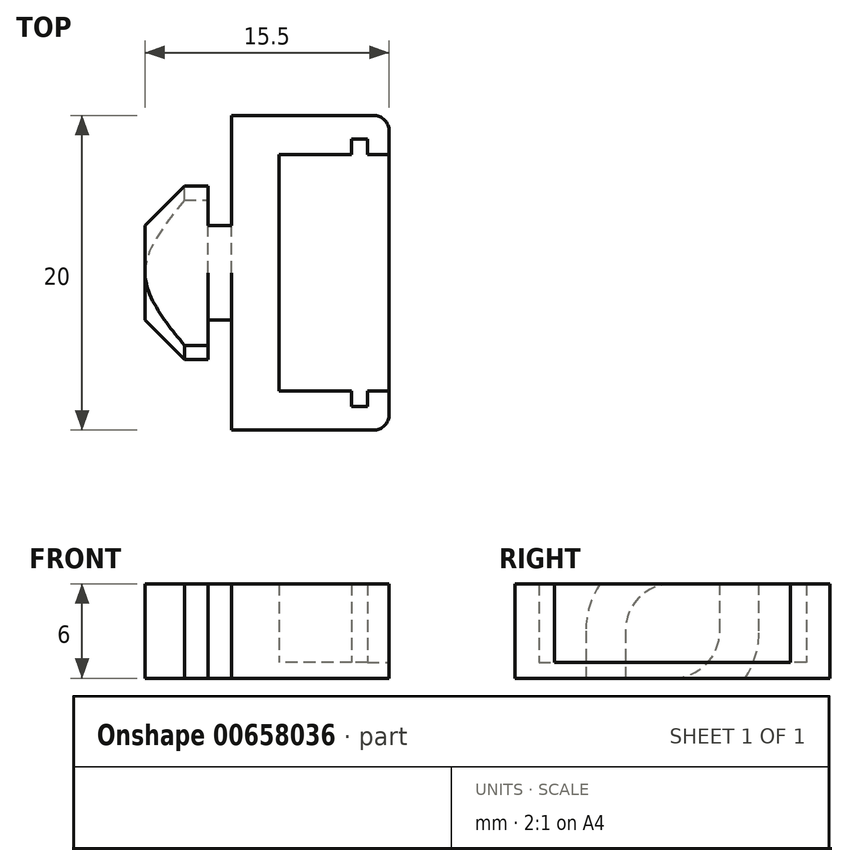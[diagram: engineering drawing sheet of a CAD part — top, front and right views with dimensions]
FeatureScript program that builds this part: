
annotation { "Feature Type Name" : "Feature", "Feature Type Description" : "" }
export const myFeature = defineFeature(function(context is Context, id is Id, definition is map)
    precondition{}
    {
        {
            var Q0;
            Q0=qCreatedBy(makeId("Top.planeOp"),FACE);
            var sketch = newSketch(context, id + "F0", { "sketchPlane" : qUnion([Q0])});
            skLineSegment(sketch, "E0.bottom", {"start": v(0, 0) * mm, "end": v(9, 0) * mm});
            skLineSegment(sketch, "E0.top", {"start": v(0, 20) * mm, "end": v(9, 20) * mm});
            skLineSegment(sketch, "E0.left", {"start": v(0, 0) * mm, "end": v(0, 7) * mm});
            skLineSegment(sketch, "E0.right", {"start": v(10, 1) * mm, "end": v(10, 2.5) * mm});
            skLineSegment(sketch, "E1", {"start": v(10, 17.5) * mm, "end": v(8.62, 17.5) * mm});
            skLineSegment(sketch, "E2", {"start": v(3, 17.5) * mm, "end": v(3, 2.5) * mm});
            skLineSegment(sketch, "E3", {"start": v(3, 2.5) * mm, "end": v(7.62, 2.5) * mm});
            skLineSegment(sketch, "E4.trimOffspring", {"start": v(10, 17.5) * mm, "end": v(10, 19) * mm});
            skLineSegment(sketch, "E5", {"start": v(7.62, 17.5) * mm, "end": v(7.62, 18.5) * mm});
            skLineSegment(sketch, "E6", {"start": v(7.62, 18.5) * mm, "end": v(8.62, 18.5) * mm});
            skLineSegment(sketch, "E7", {"start": v(8.62, 18.5) * mm, "end": v(8.62, 17.5) * mm});
            skLineSegment(sketch, "E8", {"start": v(8.62, 2.5) * mm, "end": v(8.62, 1.5) * mm});
            skLineSegment(sketch, "E9", {"start": v(8.62, 1.5) * mm, "end": v(7.62, 1.5) * mm});
            skLineSegment(sketch, "E10", {"start": v(7.62, 1.5) * mm, "end": v(7.62, 2.5) * mm});
            skLineSegment(sketch, "E11.trimOffspring", {"start": v(7.62, 17.5) * mm, "end": v(3, 17.5) * mm});
            skLineSegment(sketch, "E12.trimOffspring", {"start": v(8.62, 2.5) * mm, "end": v(10, 2.5) * mm});
            skLineSegment(sketch, "E13", {"start": v(0, 10) * mm, "end": v(-9.93, 10) * mm, "construction": true});
            skLineSegment(sketch, "E14.trimOffspring", {"start": v(0, 13) * mm, "end": v(0, 20) * mm});
            skPoint(sketch, "E15.visualSharp", {"position": v(10, 20) * mm});
            skArc(sketch, "E15.filletArc", {"start": v(10, 19) * mm, "mid": v(9.7, 19.7) * mm, "end": v(9, 20) * mm});
            skPoint(sketch, "E16.visualSharp", {"position": v(10, 0) * mm});
            skArc(sketch, "E16.filletArc", {"start": v(9, 0) * mm, "mid": v(9.7, 0.3) * mm, "end": v(10, 1) * mm});
            skLineSegment(sketch, "E17", {"start": v(0, 13) * mm, "end": v(0, 7) * mm});
            skSolve(sketch);
        }
        {
            var Q0;
            Q0 = qSketchRegion(id + "F0", true);
            extrude(context, id + "F1", {"entities" : qUnion([Q0]), "depth" : 6 * mm, "offsetDistance" : 25 * mm});
        }
        {
            var Q0;
            Q0=makeQuery(id+"F1.opExtrude","CAP_FACE",FACE,{"disambiguationData":[OSD([sQuery(id+"F0.wireOp",EDGE,"E0.bottom"),sQuery(id+"F0.wireOp",EDGE,"E0.top"),sQuery(id+"F0.wireOp",EDGE,"E0.left"),sQuery(id+"F0.wireOp",EDGE,"E0.right"),sQuery(id+"F0.wireOp",EDGE,"E1"),sQuery(id+"F0.wireOp",EDGE,"E2"),sQuery(id+"F0.wireOp",EDGE,"E3"),sQuery(id+"F0.wireOp",EDGE,"E4.trimOffspring"),sQuery(id+"F0.wireOp",EDGE,"E5"),sQuery(id+"F0.wireOp",EDGE,"E6"),sQuery(id+"F0.wireOp",EDGE,"E7"),sQuery(id+"F0.wireOp",EDGE,"E8"),sQuery(id+"F0.wireOp",EDGE,"E9"),sQuery(id+"F0.wireOp",EDGE,"E10"),sQuery(id+"F0.wireOp",EDGE,"E11.trimOffspring"),sQuery(id+"F0.wireOp",EDGE,"E12.trimOffspring"),sQuery(id+"F0.wireOp",EDGE,"jv9KcFUN-Atds-0cCT-goXF-Zrk2UxMKRZbR"),sQuery(id+"F0.wireOp",EDGE,"ZkoiLdyh-GUQE-vfzN-Ham5-BxCgyxzIEWSV"),sQuery(id+"F0.wireOp",EDGE,"btiURf1G-N151-pCzb-QpJF-9wpKFst7e4nz"),sQuery(id+"F0.wireOp",EDGE,"hKsFiE7X-pinb-RKSS-3bgO-apC7KsvpvUyI"),sQuery(id+"F0.wireOp",EDGE,"P1iatFsd-CWIg-5ysL-fost-DomH9DS6t1Jf"),sQuery(id+"F0.wireOp",EDGE,"ce11fe20-e6b6-4d68-981c-100fc1e5995b0.MirrorCS"),sQuery(id+"F0.wireOp",EDGE,"ce11fe20-e6b6-4d68-981c-100fc1e5995b1.MirrorCS"),sQuery(id+"F0.wireOp",EDGE,"ce11fe20-e6b6-4d68-981c-100fc1e5995b2.MirrorCS"),sQuery(id+"F0.wireOp",EDGE,"ce11fe20-e6b6-4d68-981c-100fc1e5995b3.MirrorCS"),sQuery(id+"F0.wireOp",EDGE,"ce11fe20-e6b6-4d68-981c-100fc1e5995b4.MirrorCS"),sQuery(id+"F0.wireOp",EDGE,"E14.trimOffspring"),sQuery(id+"F0.wireOp",EDGE,"E15.filletArc"),sQuery(id+"F0.wireOp",EDGE,"E16.filletArc")])],"isStart":true});
            var sketch = newSketch(context, id + "F2", { "sketchPlane" : qUnion([Q0])});
            skLineSegment(sketch, "E18", {"start": v(10, -1) * mm, "end": v(10, -19) * mm});
            skLineSegment(sketch, "E19", {"start": v(0, -20) * mm, "end": v(0, 0) * mm});
            skPoint(sketch, "E20.visualSharp", {"position": v(10, -20) * mm});
            skPoint(sketch, "E21.visualSharp", {"position": v(10, 0) * mm});
            skLineSegment(sketch, "E22", {"start": v(0, -20) * mm, "end": v(9, -20) * mm});
            skLineSegment(sketch, "E23", {"start": v(0, 0) * mm, "end": v(9, 0) * mm});
            skArc(sketch, "E24.filletArc", {"start": v(10, -1) * mm, "mid": v(9.7, -0.3) * mm, "end": v(9, 0) * mm});
            skArc(sketch, "E25.filletArc", {"start": v(9, -20) * mm, "mid": v(9.7, -19.7) * mm, "end": v(10, -19) * mm});
            skSolve(sketch);
        }
        {
            var Q0;
            Q0 = qSketchRegion(id + "F2", true);
            extrude(context, id + "F3", {"entities" : qUnion([Q0]), "operationType" : NewBodyOperationType.ADD, "oppositeDirection" : true, "depth" : 1 * mm, "offsetDistance" : 25 * mm});
        }
        {
            var Q0;
            Q0=makeQuery(id+"F1.opExtrude","CAP_FACE",FACE,{"disambiguationData":[OSD([sQuery(id+"F0.wireOp",EDGE,"E0.bottom"),sQuery(id+"F0.wireOp",EDGE,"E0.top"),sQuery(id+"F0.wireOp",EDGE,"E0.left"),sQuery(id+"F0.wireOp",EDGE,"E0.right"),sQuery(id+"F0.wireOp",EDGE,"E1"),sQuery(id+"F0.wireOp",EDGE,"E2"),sQuery(id+"F0.wireOp",EDGE,"E3"),sQuery(id+"F0.wireOp",EDGE,"E4.trimOffspring"),sQuery(id+"F0.wireOp",EDGE,"E5"),sQuery(id+"F0.wireOp",EDGE,"E6"),sQuery(id+"F0.wireOp",EDGE,"E7"),sQuery(id+"F0.wireOp",EDGE,"E8"),sQuery(id+"F0.wireOp",EDGE,"E9"),sQuery(id+"F0.wireOp",EDGE,"E10"),sQuery(id+"F0.wireOp",EDGE,"E11.trimOffspring"),sQuery(id+"F0.wireOp",EDGE,"E12.trimOffspring"),sQuery(id+"F0.wireOp",EDGE,"jv9KcFUN-Atds-0cCT-goXF-Zrk2UxMKRZbR"),sQuery(id+"F0.wireOp",EDGE,"ZkoiLdyh-GUQE-vfzN-Ham5-BxCgyxzIEWSV"),sQuery(id+"F0.wireOp",EDGE,"btiURf1G-N151-pCzb-QpJF-9wpKFst7e4nz"),sQuery(id+"F0.wireOp",EDGE,"hKsFiE7X-pinb-RKSS-3bgO-apC7KsvpvUyI"),sQuery(id+"F0.wireOp",EDGE,"P1iatFsd-CWIg-5ysL-fost-DomH9DS6t1Jf"),sQuery(id+"F0.wireOp",EDGE,"ce11fe20-e6b6-4d68-981c-100fc1e5995b0.MirrorCS"),sQuery(id+"F0.wireOp",EDGE,"ce11fe20-e6b6-4d68-981c-100fc1e5995b1.MirrorCS"),sQuery(id+"F0.wireOp",EDGE,"ce11fe20-e6b6-4d68-981c-100fc1e5995b2.MirrorCS"),sQuery(id+"F0.wireOp",EDGE,"ce11fe20-e6b6-4d68-981c-100fc1e5995b3.MirrorCS"),sQuery(id+"F0.wireOp",EDGE,"ce11fe20-e6b6-4d68-981c-100fc1e5995b4.MirrorCS"),sQuery(id+"F0.wireOp",EDGE,"E14.trimOffspring"),sQuery(id+"F0.wireOp",EDGE,"E15.filletArc"),sQuery(id+"F0.wireOp",EDGE,"E16.filletArc")])],"isStart":true});
            cPlane(context, id + "F4", {"entities" : qUnion([Q0]), "cplaneType" : CPlaneType.OFFSET, "offset" : 3 * mm, "oppositeDirection" : true, "width" : 150 * mm, "height" : 150 * mm});
        }
        {
            var Q0;
            Q0=qCreatedBy(id+"F4.planeOp",FACE);
            var sketch = newSketch(context, id + "F5", { "sketchPlane" : qUnion([Q0])});
            skLineSegment(sketch, "E26", {"start": v(-5.5, -10) * mm, "end": v(-5.5, -7) * mm});
            skLineSegment(sketch, "E27", {"start": v(-5.5, -7) * mm, "end": v(-3, -4.5) * mm});
            skLineSegment(sketch, "E28", {"start": v(-3, -4.5) * mm, "end": v(-1.5, -4.5) * mm});
            skLineSegment(sketch, "E29", {"start": v(-1.5, -4.5) * mm, "end": v(-1.5, -7) * mm});
            skLineSegment(sketch, "E30", {"start": v(-1.5, -7) * mm, "end": v(0, -7) * mm});
            skLineSegment(sketch, "E31", {"start": v(0, -7) * mm, "end": v(0, -10) * mm});
            skLineSegment(sketch, "E32", {"start": v(0, -10) * mm, "end": v(-5.5, -10) * mm});
            skSolve(sketch);
        }
        {
            var Q0;
            Q0 = qSketchRegion(id + "F5", true);
            var Q1;
            Q1=sQuery(id+"F5.wireOp",EDGE,"E26");
            var Q2;
            Q2=sQuery(id+"F5.wireOp",EDGE,"E27");
            var Q3;
            Q3=sQuery(id+"F5.wireOp",EDGE,"E28");
            var Q4;
            Q4=sQuery(id+"F5.wireOp",EDGE,"E29");
            var Q5;
            Q5=sQuery(id+"F5.wireOp",EDGE,"E30");
            var Q6;
            Q6=sQuery(id+"F5.wireOp",EDGE,"E32");
            revolve(context, id + "F6", {"operationType" : NewBodyOperationType.ADD, "surfaceOperationType" : NewSurfaceOperationType.NEW, "entities" : qUnion([Q0]), "surfaceEntities" : qUnion([Q1, Q2, Q3, Q4, Q5]), "axis" : qUnion([Q6]), "revolveType" : RevolveType.FULL});
        }
        {
            var Q0;
            Q0=makeQuery(id+"F6.opRevolve","SWEPT_FACE",FACE,{"disambiguationData":[OSD([sQuery(id+"F5.wireOp",EDGE,"E26")])]});
            var sketch = newSketch(context, id + "F7", { "sketchPlane" : qUnion([Q0])});
            skLineSegment(sketch, "E33.bottom", {"start": v(15.82, 0) * mm, "end": v(-26.29, 0) * mm});
            skLineSegment(sketch, "E33.top", {"start": v(15.82, -2.77) * mm, "end": v(-26.29, -2.77) * mm});
            skLineSegment(sketch, "E33.left", {"start": v(15.82, 0) * mm, "end": v(15.82, -2.77) * mm});
            skLineSegment(sketch, "E33.right", {"start": v(-26.29, 0) * mm, "end": v(-26.29, -2.77) * mm});
            skLineSegment(sketch, "E34.bottom", {"start": v(16.08, 6) * mm, "end": v(-27.21, 6) * mm});
            skLineSegment(sketch, "E34.top", {"start": v(16.08, 8.6) * mm, "end": v(-27.21, 8.6) * mm});
            skLineSegment(sketch, "E34.left", {"start": v(16.08, 6) * mm, "end": v(16.08, 8.6) * mm});
            skLineSegment(sketch, "E34.right", {"start": v(-27.21, 6) * mm, "end": v(-27.21, 8.6) * mm});
            skSolve(sketch);
        }
        {
            var Q0;
            Q0 = qSketchRegion(id + "F7", true);
            extrude(context, id + "F8", {"entities" : qUnion([Q0]), "operationType" : NewBodyOperationType.REMOVE, "oppositeDirection" : true, "depth" : 25 * mm, "offsetDistance" : 25 * mm});
        }
        {
            var Q0;
            Q0=makeQuery(id+"F8.boolean.opBoolean","COPY",FACE,{"derivedFrom":makeQuery(id+"F8.opExtrude","SWEPT_FACE",FACE,{"disambiguationData":[OSD([sQuery(id+"F7.wireOp",EDGE,"E33.bottom")])]})});
            var sketch = newSketch(context, id + "F9", { "sketchPlane" : qUnion([Q0])});
            skLineSegment(sketch, "E35", {"start": v(-5.5, -10) * mm, "end": v(-5.5, -7) * mm});
            skLineSegment(sketch, "E36", {"start": v(-5.5, -7) * mm, "end": v(-3, -4.5) * mm});
            skLineSegment(sketch, "E37", {"start": v(-3, -4.5) * mm, "end": v(-1.5, -4.5) * mm});
            skLineSegment(sketch, "E38", {"start": v(-1.5, -4.5) * mm, "end": v(-1.5, -7) * mm});
            skLineSegment(sketch, "E39", {"start": v(-1.5, -7) * mm, "end": v(0, -7) * mm});
            skLineSegment(sketch, "E40", {"start": v(0, -7) * mm, "end": v(0, -10) * mm});
            skLineSegment(sketch, "E41", {"start": v(0, -10) * mm, "end": v(-5.5, -10) * mm});
            skSolve(sketch);
        }
        {
            var Q0;
            Q0 = qSketchRegion(id + "F9", true);
            extrude(context, id + "F10", {"entities" : qUnion([Q0]), "operationType" : NewBodyOperationType.ADD, "oppositeDirection" : true, "depth" : 3 * mm, "offsetDistance" : 25 * mm});
        }
        {
            var Q0;
            Q0=makeQuery(id+"F8.boolean.opBoolean","COPY",FACE,{"derivedFrom":makeQuery(id+"F8.opExtrude","SWEPT_FACE",FACE,{"disambiguationData":[OSD([sQuery(id+"F7.wireOp",EDGE,"E34.bottom")])]})});
            var sketch = newSketch(context, id + "F11", { "sketchPlane" : qUnion([Q0])});
            skLineSegment(sketch, "E42", {"start": v(-5.5, 10) * mm, "end": v(-5.5, 13) * mm});
            skLineSegment(sketch, "E43", {"start": v(-5.5, 13) * mm, "end": v(-3, 15.5) * mm});
            skLineSegment(sketch, "E44", {"start": v(-3, 15.5) * mm, "end": v(-1.5, 15.5) * mm});
            skLineSegment(sketch, "E45", {"start": v(-1.5, 15.5) * mm, "end": v(-1.5, 13) * mm});
            skLineSegment(sketch, "E46", {"start": v(-1.5, 13) * mm, "end": v(0, 13) * mm});
            skLineSegment(sketch, "E47", {"start": v(0, 13) * mm, "end": v(0, 10) * mm});
            skLineSegment(sketch, "E48", {"start": v(0, 10) * mm, "end": v(-5.5, 10) * mm});
            skSolve(sketch);
        }
        {
            var Q0;
            Q0 = qSketchRegion(id + "F11", true);
            extrude(context, id + "F12", {"entities" : qUnion([Q0]), "operationType" : NewBodyOperationType.ADD, "oppositeDirection" : true, "depth" : 3 * mm, "offsetDistance" : 25 * mm});
        }
    });
